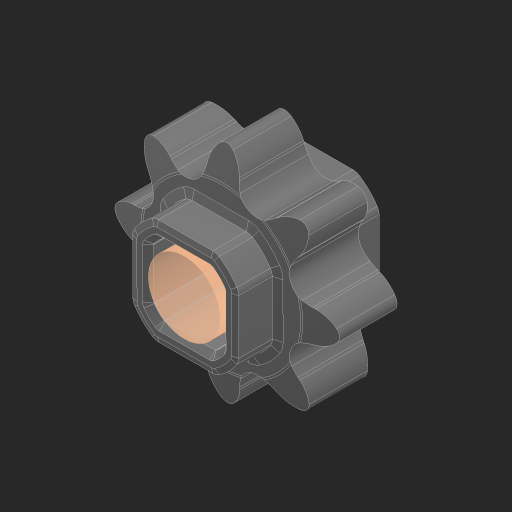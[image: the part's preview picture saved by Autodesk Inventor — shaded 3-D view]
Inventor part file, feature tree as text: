
AUTODESK INVENTOR PART (.ipt)
format: ipt  version: 2023 (Build 270158000, 158)  size: 564,736 bytes
history: native  units: in
note: dims shown in document units (in); Inventor stores cm internally (conversion verified against a paired STEP export)
features: move_body x1, sketch x1, other x1, fillet x1, extrude x1
ambient origin geometry x8: Origin, YZ Plane, XZ Plane, XY Plane, X Axis, Y Axis, Z Axis, Center Point
bodies: Solid1 (feature_tree)
feature tree (5):
  move_body  "Move Body1"
  sketch  "Sketch1"  dims[d1=0.3937in d2=0.0in d3=0.1535in]
  other  "Srf1"
  fillet  "Fillet6"  Radius=0.25in
  extrude  "ExtrusionSrf1"  Depth=0.3937in
